# Revit family: Plumbing-Fixtures_Grohe_Grohtherm_Smart-Control_29119000_14_METRIC1
name_source: partatom
category: Plumbing Fixtures
revit_build: Autodesk Revit 2015 (Build: 20160512_1515(x64)
units: mm (PartAtom-declared; Revit-internal decimal feet)

## types (1)
- 29119000
    ADA Compliant = No
    Assembly Code = C1030220
    AssetType = Fixed
    CW Connection = Yes
    CWFU = 4.5
    ClassificationName = Uniclass 2015
    ClassificationValue = Pr_65_54_95_88
    Cold Water Connection Diameter = 10 mm  [stored 0.0328084 ft]
    Color = Chrome
    Cost = 0 $
    Default Elevation = 0 mm  [stored 0 ft]
    DurationUnit = Years
    Ecojoy = Yes
    ExpectedLife = 0
    Faucet Material = Grohe-Chrome-Polished
    Finish = Chrome
    HW Connection = Yes
    HWFU = 4.5
    Hot Water Connection Diameter = 10 mm  [stored 0.0328084 ft]
    Keynote = N13
    Low Emitting Material = No
    Manufacturer = Grohe Limited
    Masterformat Number = 01 52 19
    Masterformat Title = Sanitary Facilities
    Material = Chrome
    Model = Grohtherm - Smart Control Thermostatic Mixer
    ModelNumber = Grohtherm - 29119000
    NBSDescription = Thermostatic mixing valves
    NBSObjectName = Thermostatic mixing valves
    NBSReference = 90-10-90/370
    ProductionYear = 2016
    Type Comments = Grohtherm - 29119000
    TypeName = Grohtherm - Smart Control Thermostatic Mixer
    URL = www.grohe.com
    Vent Connection = No
    WFU = 0
    WarrantyDurationUnit = Years
    Waste Connection = No
    _BIMspec_GUID = 0
    _current revision = 1
    _distributed by = www.bimstore.co.uk

note: [stored X ft] marks values corroborated as IEEE doubles in the binary element streams (Revit-internal decimal feet)

## geometry (parser evidence)
native form markers: Blend x6, Sweep x2
no freeform markers — native parametric forms only
